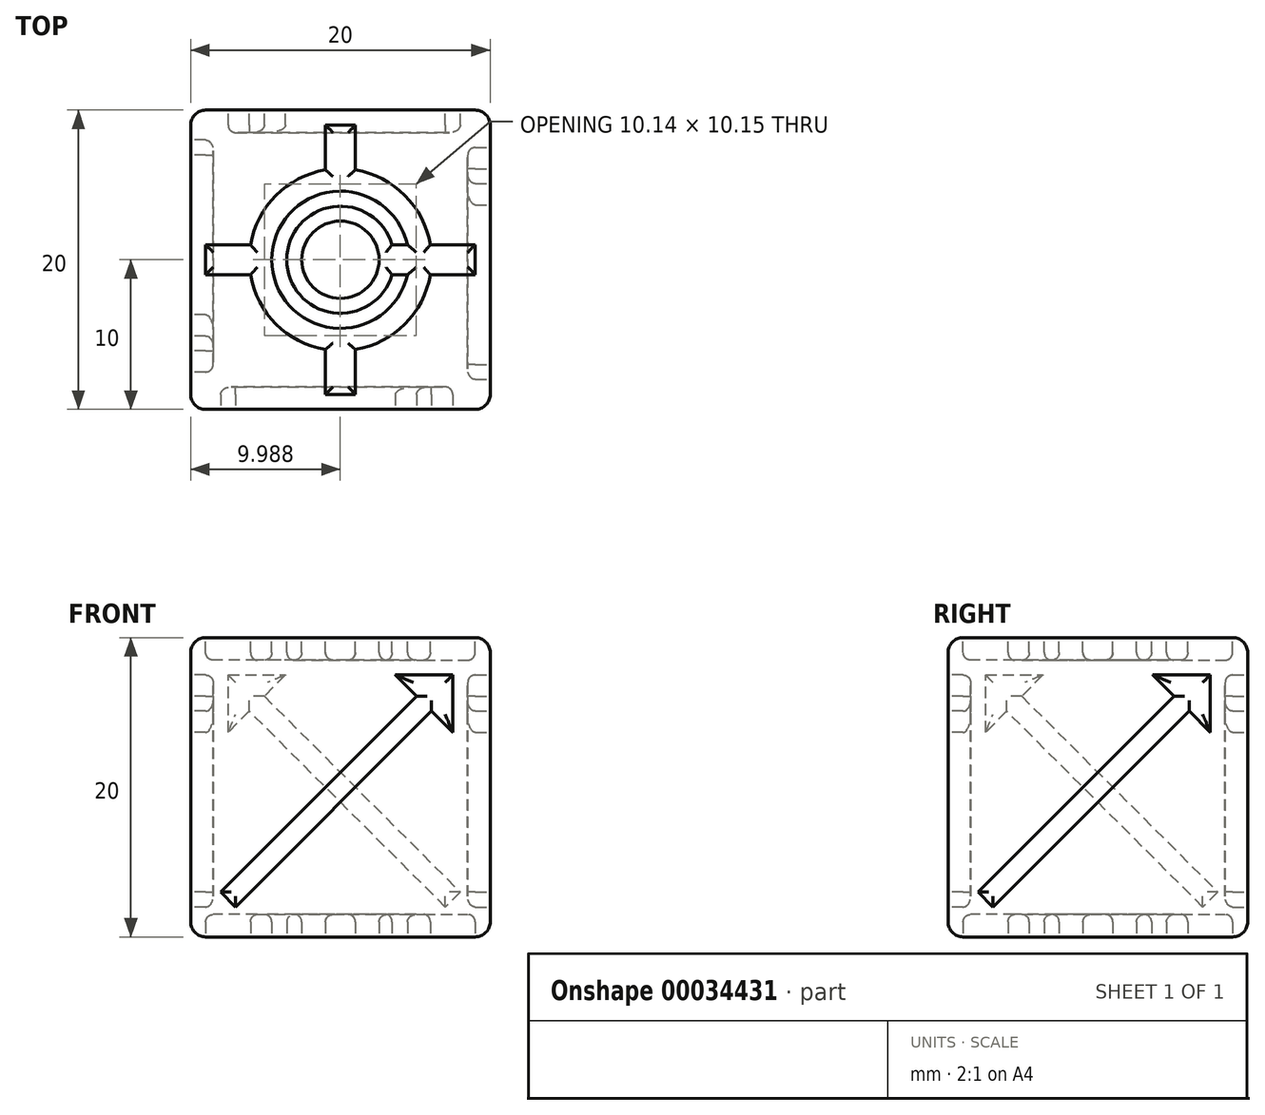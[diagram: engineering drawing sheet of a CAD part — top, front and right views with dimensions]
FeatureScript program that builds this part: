
annotation { "Feature Type Name" : "Feature", "Feature Type Description" : "" }
export const myFeature = defineFeature(function(context is Context, id is Id, definition is map)
    precondition{}
    {
        {
            var Q0;
            Q0=qCreatedBy(makeId("Top.planeOp"),FACE);
            var sketch = newSketch(context, id + "F0", { "sketchPlane" : qUnion([Q0])});
            skLineSegment(sketch, "E0.rect.bottom", {"start": v(10, -10) * mm, "end": v(-10, -10) * mm});
            skLineSegment(sketch, "E0.rect.top", {"start": v(10, 10) * mm, "end": v(-10, 10) * mm});
            skLineSegment(sketch, "E0.rect.left", {"start": v(10, -10) * mm, "end": v(10, 10) * mm});
            skLineSegment(sketch, "E0.rect.right", {"start": v(-10, -10) * mm, "end": v(-10, 10) * mm});
            skPoint(sketch, "E0.rect.middle", {"position": v(0, 0) * mm});
            skLineSegment(sketch, "E1", {"start": v(0, 10) * mm, "end": v(0, -10) * mm, "construction": true});
            skLineSegment(sketch, "E2", {"start": v(-10, 0) * mm, "end": v(10, 0) * mm, "construction": true});
            skSolve(sketch);
        }
        {
            var Q0;
            Q0=makeQuery(id+"F0.imprint","IMPRINT",FACE,{"disambiguationData":[TD([[makeQuery(id+"F0.imprint","IMPRINT",EDGE,{"derivedFrom":sQuery(id+"F0.wireOp",EDGE,"E0.rect.bottom")}),-1.0]])]});
            extrude(context, id + "F1", {"entities" : qUnion([Q0]), "endBound" : BoundingType.SYMMETRIC, "depth" : 20 * mm});
        }
        {
            var Q0;
            Q0=makeQuery(id+"F1.opExtrude","CAP_FACE",FACE,{"disambiguationData":[OSD([sQuery(id+"F0.wireOp",EDGE,"E0.rect.bottom"),sQuery(id+"F0.wireOp",EDGE,"E0.rect.top"),sQuery(id+"F0.wireOp",EDGE,"E0.rect.left"),sQuery(id+"F0.wireOp",EDGE,"E0.rect.right")])],"isStart":false});
            var sketch = newSketch(context, id + "F2", { "sketchPlane" : qUnion([Q0])});
            skLineSegment(sketch, "E3", {"start": v(-3.67, 7.5) * mm, "end": v(-7.5, 7.5) * mm});
            skLineSegment(sketch, "E4", {"start": v(-7.5, 7.5) * mm, "end": v(-7.5, 3.67) * mm});
            skLineSegment(sketch, "E5", {"start": v(-7.5, 3.67) * mm, "end": v(-6.09, 5.09) * mm});
            skLineSegment(sketch, "E6", {"start": v(-6.09, 5.09) * mm, "end": v(7, -8) * mm});
            skLineSegment(sketch, "E7", {"start": v(7, -8) * mm, "end": v(8, -7) * mm});
            skLineSegment(sketch, "E8", {"start": v(8, -7) * mm, "end": v(-5.09, 6.09) * mm});
            skLineSegment(sketch, "E9", {"start": v(-5.09, 6.09) * mm, "end": v(-3.67, 7.5) * mm});
            skLineSegment(sketch, "E10", {"start": v(-7.5, 7.5) * mm, "end": v(7.5, -7.5) * mm, "construction": true});
            skSolve(sketch);
        }
        {
            var Q0;
            Q0=makeQuery(id+"F2.imprint","IMPRINT",FACE,{"disambiguationData":[TD([[makeQuery(id+"F2.imprint","IMPRINT",EDGE,{"derivedFrom":sQuery(id+"F2.wireOp",EDGE,"E3")}),1.0]])]});
            extrude(context, id + "F3", {"entities" : qUnion([Q0]), "oppositeDirection" : true, "depth" : 1.5 * mm});
        }
        {
            var Q0;
            Q0=makeQuery(id+"F3.opExtrude","SWEPT_BODY",BODY,{"disambiguationData":[OSD([sQuery(id+"F2.wireOp",EDGE,"E3"),sQuery(id+"F2.wireOp",EDGE,"E4"),sQuery(id+"F2.wireOp",EDGE,"E5"),sQuery(id+"F2.wireOp",EDGE,"E6"),sQuery(id+"F2.wireOp",EDGE,"E7"),sQuery(id+"F2.wireOp",EDGE,"E8"),sQuery(id+"F2.wireOp",EDGE,"E9")])]});
            var Q1;
            Q1=sQuery(id+"F0.wireOp",EDGE,"E2");
            circularPattern(context, id + "F4", {"operationType" : NewBodyOperationType.REMOVE, "entities" : qUnion([Q0]), "axis" : qUnion([Q1]), "angle" : 90 * degree, "instanceCount" : 4});
        }
        {
            var Q0;
            Q0=makeQuery(id+"F1.opExtrude","SWEPT_FACE",FACE,{"disambiguationData":[OSD([sQuery(id+"F0.wireOp",EDGE,"E0.rect.left")])]});
            var sketch = newSketch(context, id + "F5", { "sketchPlane" : qUnion([Q0])});
            skArc(sketch, "E11", {"start": v(-1, 6) * mm, "mid": v(-4.3, 4.3) * mm, "end": v(-6, 1) * mm});
            skArc(sketch, "E12.0", {"start": v(-1, 4.47) * mm, "mid": v(0, -4.58) * mm, "end": v(1, 4.47) * mm});
            skLineSegment(sketch, "E13.rect.top", {"start": v(1, 9) * mm, "end": v(-1, 9) * mm});
            skLineSegment(sketch, "E13.rect.left", {"start": v(1, 6) * mm, "end": v(1, 9) * mm});
            skLineSegment(sketch, "E13.rect.right", {"start": v(-1, 6) * mm, "end": v(-1, 9) * mm});
            skPoint(sketch, "E13.rect.middle", {"position": v(0, 7.5) * mm});
            skLineSegment(sketch, "E14.1.0", {"start": v(-6, 1) * mm, "end": v(-9, 1) * mm});
            skLineSegment(sketch, "E14.1.1", {"start": v(-6, -1) * mm, "end": v(-9, -1) * mm});
            skLineSegment(sketch, "E14.1.2", {"start": v(-9, 1) * mm, "end": v(-9, -1) * mm});
            skLineSegment(sketch, "E14.2.0", {"start": v(-1, -6) * mm, "end": v(-1, -9) * mm});
            skLineSegment(sketch, "E14.2.1", {"start": v(1, -6) * mm, "end": v(1, -9) * mm});
            skLineSegment(sketch, "E14.2.2", {"start": v(-1, -9) * mm, "end": v(1, -9) * mm});
            skLineSegment(sketch, "E15.1.3.0", {"start": v(6, -1) * mm, "end": v(9, -1) * mm});
            skLineSegment(sketch, "E15.3.3.0", {"start": v(6, 1) * mm, "end": v(9, 1) * mm});
            skLineSegment(sketch, "E15.6.3.0", {"start": v(9, -1) * mm, "end": v(9, 1) * mm});
            skArc(sketch, "E16.trimOffspring", {"start": v(6, 1) * mm, "mid": v(4.3, 4.3) * mm, "end": v(1, 6) * mm});
            skArc(sketch, "E17.trimOffspring", {"start": v(1, -6) * mm, "mid": v(4.3, -4.3) * mm, "end": v(6, -1) * mm});
            skArc(sketch, "E18.trimOffspring", {"start": v(-6, -1) * mm, "mid": v(-4.3, -4.3) * mm, "end": v(-1, -6) * mm});
            skArc(sketch, "E19.0", {"start": v(-1, 3.44) * mm, "mid": v(0, -3.58) * mm, "end": v(1, 3.44) * mm});
            skCircle(sketch, "E20.0", {"center": v(0, 0) * mm, "radius": 2.58 * mm});
            skLineSegment(sketch, "E21", {"start": v(-1, 4.47) * mm, "end": v(-1, 3.44) * mm});
            skLineSegment(sketch, "E22", {"start": v(1, 4.47) * mm, "end": v(1, 3.44) * mm});
            skSolve(sketch);
        }
        {
            var Q0;
            Q0=makeQuery(id+"F5.imprint","IMPRINT",FACE,{"disambiguationData":[TD([[makeQuery(id+"F5.imprint","IMPRINT",EDGE,{"derivedFrom":sQuery(id+"F5.wireOp",EDGE,"E11")}),1.0]])]});
            var Q1;
            Q1=makeQuery(id+"F5.imprint","IMPRINT",FACE,{"disambiguationData":[TD([[makeQuery(id+"F5.imprint","IMPRINT",EDGE,{"derivedFrom":sQuery(id+"F5.wireOp",EDGE,"E19.0")}),1.0]])]});
            extrude(context, id + "F6", {"entities" : qUnion([Q0, Q1]), "oppositeDirection" : true, "depth" : 1.5 * mm});
        }
        {
            var Q0;
            Q0=makeQuery(id+"F6.opExtrude","SWEPT_BODY",BODY,{"disambiguationData":[OSD([sQuery(id+"F5.wireOp",EDGE,"E11"),sQuery(id+"F5.wireOp",EDGE,"E12.0"),sQuery(id+"F5.wireOp",EDGE,"E13.rect.top"),sQuery(id+"F5.wireOp",EDGE,"E13.rect.left"),sQuery(id+"F5.wireOp",EDGE,"E13.rect.right"),sQuery(id+"F5.wireOp",EDGE,"E14.1.0"),sQuery(id+"F5.wireOp",EDGE,"E14.1.1"),sQuery(id+"F5.wireOp",EDGE,"E14.1.2"),sQuery(id+"F5.wireOp",EDGE,"E14.2.0"),sQuery(id+"F5.wireOp",EDGE,"E14.2.1"),sQuery(id+"F5.wireOp",EDGE,"E14.2.2"),sQuery(id+"F5.wireOp",EDGE,"E15.1.3.0"),sQuery(id+"F5.wireOp",EDGE,"E15.3.3.0"),sQuery(id+"F5.wireOp",EDGE,"E15.6.3.0"),sQuery(id+"F5.wireOp",EDGE,"E16.trimOffspring"),sQuery(id+"F5.wireOp",EDGE,"E17.trimOffspring"),sQuery(id+"F5.wireOp",EDGE,"E18.trimOffspring")])]});
            var Q1;
            Q1=makeQuery(id+"F6.opExtrude","SWEPT_BODY",BODY,{"disambiguationData":[OSD([sQuery(id+"F5.wireOp",EDGE,"E19.0"),sQuery(id+"F5.wireOp",EDGE,"E20.0")])]});
            var Q2;
            Q2=qCreatedBy(makeId("Right.planeOp"),FACE);
            mirror(context, id + "F7", {"operationType" : NewBodyOperationType.REMOVE, "entities" : qUnion([Q0, Q1]), "mirrorPlane" : qUnion([Q2])});
        }
        {
            var Q0;
            Q0=makeQuery(id+"F6.opExtrude","SWEPT_BODY",BODY,{"disambiguationData":[OSD([sQuery(id+"F5.wireOp",EDGE,"E19.0"),sQuery(id+"F5.wireOp",EDGE,"E20.0")])]});
            var Q1;
            Q1=makeQuery(id+"F6.opExtrude","SWEPT_BODY",BODY,{"disambiguationData":[OSD([sQuery(id+"F5.wireOp",EDGE,"E11"),sQuery(id+"F5.wireOp",EDGE,"E12.0"),sQuery(id+"F5.wireOp",EDGE,"E13.rect.top"),sQuery(id+"F5.wireOp",EDGE,"E13.rect.left"),sQuery(id+"F5.wireOp",EDGE,"E13.rect.right"),sQuery(id+"F5.wireOp",EDGE,"E14.1.0"),sQuery(id+"F5.wireOp",EDGE,"E14.1.1"),sQuery(id+"F5.wireOp",EDGE,"E14.1.2"),sQuery(id+"F5.wireOp",EDGE,"E14.2.0"),sQuery(id+"F5.wireOp",EDGE,"E14.2.1"),sQuery(id+"F5.wireOp",EDGE,"E14.2.2"),sQuery(id+"F5.wireOp",EDGE,"E15.1.3.0"),sQuery(id+"F5.wireOp",EDGE,"E15.3.3.0"),sQuery(id+"F5.wireOp",EDGE,"E15.6.3.0"),sQuery(id+"F5.wireOp",EDGE,"E16.trimOffspring"),sQuery(id+"F5.wireOp",EDGE,"E17.trimOffspring"),sQuery(id+"F5.wireOp",EDGE,"E18.trimOffspring")])]});
            var Q2;
            Q2=makeQuery(id+"F1.opExtrude","SWEPT_BODY",BODY,{"disambiguationData":[OSD([sQuery(id+"F0.wireOp",EDGE,"E0.rect.bottom"),sQuery(id+"F0.wireOp",EDGE,"E0.rect.top"),sQuery(id+"F0.wireOp",EDGE,"E0.rect.left"),sQuery(id+"F0.wireOp",EDGE,"E0.rect.right")])]});
            booleanBodies(context, id + "F8", {"operationType" : BooleanOperationType.SUBTRACTION, "tools" : qUnion([Q0, Q1]), "targets" : qUnion([Q2])});
        }
        {
            var Q0;
            Q0=makeQuery(id+"F1.opExtrude","CAP_EDGE",EDGE,{"disambiguationData":[OSD([sQuery(id+"F0.wireOp",EDGE,"E0.rect.bottom")])],"isStart":false});
            var Q1;
            Q1=makeQuery(id+"F1.opExtrude","CAP_EDGE",EDGE,{"disambiguationData":[OSD([sQuery(id+"F0.wireOp",EDGE,"E0.rect.left")])],"isStart":false});
            var Q2;
            Q2=makeQuery(id+"F1.opExtrude","SWEPT_EDGE",EDGE,{"disambiguationData":[OSD([sQuery(id+"F0.wireOp",EDGE,"E0.rect.bottom"),sQuery(id+"F0.wireOp",EDGE,"E0.rect.left")])]});
            var Q3;
            Q3=makeQuery(id+"F1.opExtrude","SWEPT_EDGE",EDGE,{"disambiguationData":[OSD([sQuery(id+"F0.wireOp",EDGE,"E0.rect.top"),sQuery(id+"F0.wireOp",EDGE,"E0.rect.left")])]});
            var Q4;
            Q4=makeQuery(id+"F1.opExtrude","SWEPT_EDGE",EDGE,{"disambiguationData":[OSD([sQuery(id+"F0.wireOp",EDGE,"E0.rect.bottom"),sQuery(id+"F0.wireOp",EDGE,"E0.rect.right")])]});
            var Q5;
            Q5=makeQuery(id+"F1.opExtrude","CAP_EDGE",EDGE,{"disambiguationData":[OSD([sQuery(id+"F0.wireOp",EDGE,"E0.rect.right")])],"isStart":false});
            var Q6;
            Q6=makeQuery(id+"F1.opExtrude","CAP_EDGE",EDGE,{"disambiguationData":[OSD([sQuery(id+"F0.wireOp",EDGE,"E0.rect.bottom")])],"isStart":true});
            var Q7;
            Q7=makeQuery(id+"F1.opExtrude","CAP_EDGE",EDGE,{"disambiguationData":[OSD([sQuery(id+"F0.wireOp",EDGE,"E0.rect.top")])],"isStart":false});
            var Q8;
            Q8=makeQuery(id+"F1.opExtrude","SWEPT_EDGE",EDGE,{"disambiguationData":[OSD([sQuery(id+"F0.wireOp",EDGE,"E0.rect.top"),sQuery(id+"F0.wireOp",EDGE,"E0.rect.right")])]});
            var Q9;
            Q9=makeQuery(id+"F1.opExtrude","CAP_EDGE",EDGE,{"disambiguationData":[OSD([sQuery(id+"F0.wireOp",EDGE,"E0.rect.top")])],"isStart":true});
            var Q10;
            Q10=makeQuery(id+"F1.opExtrude","CAP_EDGE",EDGE,{"disambiguationData":[OSD([sQuery(id+"F0.wireOp",EDGE,"E0.rect.right")])],"isStart":true});
            var Q11;
            Q11=makeQuery(id+"F1.opExtrude","CAP_EDGE",EDGE,{"disambiguationData":[OSD([sQuery(id+"F0.wireOp",EDGE,"E0.rect.left")])],"isStart":true});
            fillet(context, id + "F9", {"entities" : qUnion([Q0, Q1, Q2, Q3, Q4, Q5, Q6, Q7, Q8, Q9, Q10, Q11]), "radius" : 1 * mm, "tangentPropagation" : true, "allowEdgeOverflow" : false});
        }
        {
            var Q0;
            Q0=makeQuery(id+"F4.boolean.opBoolean","COPY",FACE,{"derivedFrom":makeQuery(id+"F4.opPattern","COPY",FACE,{"derivedFrom":makeQuery(id+"F3.opExtrude","CAP_FACE",FACE,{"disambiguationData":[OSD([sQuery(id+"F2.wireOp",EDGE,"E3"),sQuery(id+"F2.wireOp",EDGE,"E4"),sQuery(id+"F2.wireOp",EDGE,"E5"),sQuery(id+"F2.wireOp",EDGE,"E6"),sQuery(id+"F2.wireOp",EDGE,"E7"),sQuery(id+"F2.wireOp",EDGE,"E8"),sQuery(id+"F2.wireOp",EDGE,"E9")])],"isStart":false}),"instanceName":"1"})});
            var Q1;
            Q1=makeQuery(id+"F8.opBoolean","COPY",FACE,{"derivedFrom":makeQuery(id+"F6.opExtrude","CAP_FACE",FACE,{"disambiguationData":[OSD([sQuery(id+"F5.wireOp",EDGE,"E19.0"),sQuery(id+"F5.wireOp",EDGE,"E20.0")])],"isStart":false})});
            var Q2;
            Q2=makeQuery(id+"F8.opBoolean","COPY",FACE,{"derivedFrom":makeQuery(id+"F6.opExtrude","CAP_FACE",FACE,{"disambiguationData":[OSD([sQuery(id+"F5.wireOp",EDGE,"E11"),sQuery(id+"F5.wireOp",EDGE,"E12.0"),sQuery(id+"F5.wireOp",EDGE,"E13.rect.top"),sQuery(id+"F5.wireOp",EDGE,"E13.rect.left"),sQuery(id+"F5.wireOp",EDGE,"E13.rect.right"),sQuery(id+"F5.wireOp",EDGE,"E14.1.0"),sQuery(id+"F5.wireOp",EDGE,"E14.1.1"),sQuery(id+"F5.wireOp",EDGE,"E14.1.2"),sQuery(id+"F5.wireOp",EDGE,"E14.2.0"),sQuery(id+"F5.wireOp",EDGE,"E14.2.1"),sQuery(id+"F5.wireOp",EDGE,"E14.2.2"),sQuery(id+"F5.wireOp",EDGE,"E15.1.3.0"),sQuery(id+"F5.wireOp",EDGE,"E15.3.3.0"),sQuery(id+"F5.wireOp",EDGE,"E15.6.3.0"),sQuery(id+"F5.wireOp",EDGE,"E16.trimOffspring"),sQuery(id+"F5.wireOp",EDGE,"E17.trimOffspring"),sQuery(id+"F5.wireOp",EDGE,"E18.trimOffspring")])],"isStart":false})});
            var Q3;
            Q3=makeQuery(id+"F4.boolean.opBoolean","COPY",FACE,{"derivedFrom":makeQuery(id+"F3.opExtrude","CAP_FACE",FACE,{"disambiguationData":[OSD([sQuery(id+"F2.wireOp",EDGE,"E3"),sQuery(id+"F2.wireOp",EDGE,"E4"),sQuery(id+"F2.wireOp",EDGE,"E5"),sQuery(id+"F2.wireOp",EDGE,"E6"),sQuery(id+"F2.wireOp",EDGE,"E7"),sQuery(id+"F2.wireOp",EDGE,"E8"),sQuery(id+"F2.wireOp",EDGE,"E9")])],"isStart":false})});
            var Q4;
            Q4=makeQuery(id+"F4.boolean.opBoolean","COPY",FACE,{"derivedFrom":makeQuery(id+"F4.opPattern","COPY",FACE,{"derivedFrom":makeQuery(id+"F3.opExtrude","CAP_FACE",FACE,{"disambiguationData":[OSD([sQuery(id+"F2.wireOp",EDGE,"E3"),sQuery(id+"F2.wireOp",EDGE,"E4"),sQuery(id+"F2.wireOp",EDGE,"E5"),sQuery(id+"F2.wireOp",EDGE,"E6"),sQuery(id+"F2.wireOp",EDGE,"E7"),sQuery(id+"F2.wireOp",EDGE,"E8"),sQuery(id+"F2.wireOp",EDGE,"E9")])],"isStart":false}),"instanceName":"3"})});
            var Q5;
            Q5=makeQuery(id+"F7.boolean.opBoolean","COPY",FACE,{"derivedFrom":makeQuery(id+"F7.opPattern","COPY",FACE,{"derivedFrom":makeQuery(id+"F6.opExtrude","CAP_FACE",FACE,{"disambiguationData":[OSD([sQuery(id+"F5.wireOp",EDGE,"E11"),sQuery(id+"F5.wireOp",EDGE,"E12.0"),sQuery(id+"F5.wireOp",EDGE,"E13.rect.top"),sQuery(id+"F5.wireOp",EDGE,"E13.rect.left"),sQuery(id+"F5.wireOp",EDGE,"E13.rect.right"),sQuery(id+"F5.wireOp",EDGE,"E14.1.0"),sQuery(id+"F5.wireOp",EDGE,"E14.1.1"),sQuery(id+"F5.wireOp",EDGE,"E14.1.2"),sQuery(id+"F5.wireOp",EDGE,"E14.2.0"),sQuery(id+"F5.wireOp",EDGE,"E14.2.1"),sQuery(id+"F5.wireOp",EDGE,"E14.2.2"),sQuery(id+"F5.wireOp",EDGE,"E15.1.3.0"),sQuery(id+"F5.wireOp",EDGE,"E15.3.3.0"),sQuery(id+"F5.wireOp",EDGE,"E15.6.3.0"),sQuery(id+"F5.wireOp",EDGE,"E16.trimOffspring"),sQuery(id+"F5.wireOp",EDGE,"E17.trimOffspring"),sQuery(id+"F5.wireOp",EDGE,"E18.trimOffspring")])],"isStart":false}),"instanceName":"1"})});
            var Q6;
            Q6=makeQuery(id+"F7.boolean.opBoolean","COPY",FACE,{"derivedFrom":makeQuery(id+"F7.opPattern","COPY",FACE,{"derivedFrom":makeQuery(id+"F6.opExtrude","CAP_FACE",FACE,{"disambiguationData":[OSD([sQuery(id+"F5.wireOp",EDGE,"E19.0"),sQuery(id+"F5.wireOp",EDGE,"E20.0")])],"isStart":false}),"instanceName":"1"})});
            var Q7;
            Q7=makeQuery(id+"F4.boolean.opBoolean","COPY",FACE,{"derivedFrom":makeQuery(id+"F4.opPattern","COPY",FACE,{"derivedFrom":makeQuery(id+"F3.opExtrude","CAP_FACE",FACE,{"disambiguationData":[OSD([sQuery(id+"F2.wireOp",EDGE,"E3"),sQuery(id+"F2.wireOp",EDGE,"E4"),sQuery(id+"F2.wireOp",EDGE,"E5"),sQuery(id+"F2.wireOp",EDGE,"E6"),sQuery(id+"F2.wireOp",EDGE,"E7"),sQuery(id+"F2.wireOp",EDGE,"E8"),sQuery(id+"F2.wireOp",EDGE,"E9")])],"isStart":false}),"instanceName":"2"})});
            fillet(context, id + "F10", {"entities" : qUnion([Q0, Q1, Q2, Q3, Q4, Q5, Q6, Q7]), "radius" : 0.5 * mm, "tangentPropagation" : true, "allowEdgeOverflow" : false});
        }
        {
            var Q0;
            Q0=makeQuery(id+"F1.opExtrude","SWEPT_BODY",BODY,{"disambiguationData":[OSD([sQuery(id+"F0.wireOp",EDGE,"E0.rect.bottom"),sQuery(id+"F0.wireOp",EDGE,"E0.rect.top"),sQuery(id+"F0.wireOp",EDGE,"E0.rect.left"),sQuery(id+"F0.wireOp",EDGE,"E0.rect.right")])]});
            var Q1;
            Q1=sQuery(id+"F0.wireOp",EDGE,"E1");
            transform(context, id + "F11", {"entities" : qUnion([Q0]), "transformType" : TransformType.ROTATION, "transformAxis" : qUnion([Q1]), "angle" : 90 * degree, "oppositeDirection" : true, "makeCopy" : false});
        }
    });
